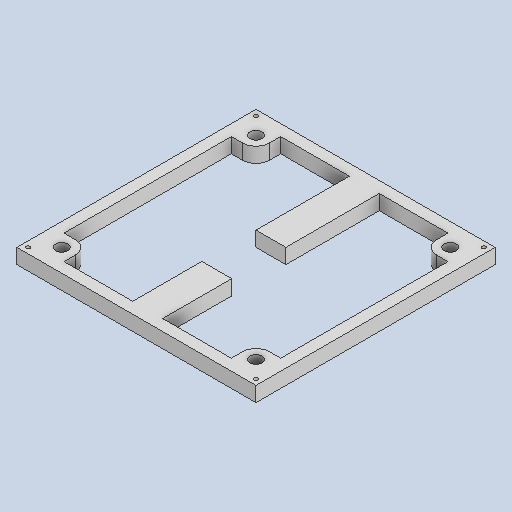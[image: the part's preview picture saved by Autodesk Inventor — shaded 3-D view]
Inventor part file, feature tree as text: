
AUTODESK INVENTOR PART (.ipt)
format: ipt  version: 2024 (Build 280153000, 153)  size: 349,696 bytes
history: native  units: in
note: dims shown in document units (in); Inventor stores cm internally (conversion verified against a paired STEP export)
features: extrude x2, projected_geometry x2
ambient origin geometry x8: Origin, YZ Plane, XZ Plane, XY Plane, X Axis, Y Axis, Z Axis, Center Point
bodies: Solid1 (feature_tree)
feature tree (4):
  extrude  "Extrusion1"  Depth=4.0in
  extrude  "Extrusion2"  Depth=4.0in
  projected_geometry  "Projected Loop1"
  projected_geometry  "Projected Loop2"
